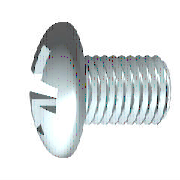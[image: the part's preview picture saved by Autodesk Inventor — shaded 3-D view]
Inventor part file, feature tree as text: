
AUTODESK INVENTOR PART (.ipt)
format: ipt  version: 2020 (Build 240168000, 168)  size: 282,112 bytes
history: native  units: mm (DEFAULTED — no unit token found)
features: other x2, plane x2, extrude x1
ambient origin geometry x7: Origin, YZ Plane, XZ Plane, X Axis, Y Axis, Z Axis, Center Point
bodies: Solid1 (feature_tree)
feature tree (5):
  other  "Базовый элемент"
  plane  "Work Plane1"
  extrude  "Паз"  Depth=4.0mm
  other  "Вырез"
  plane  "Work Plane3"
